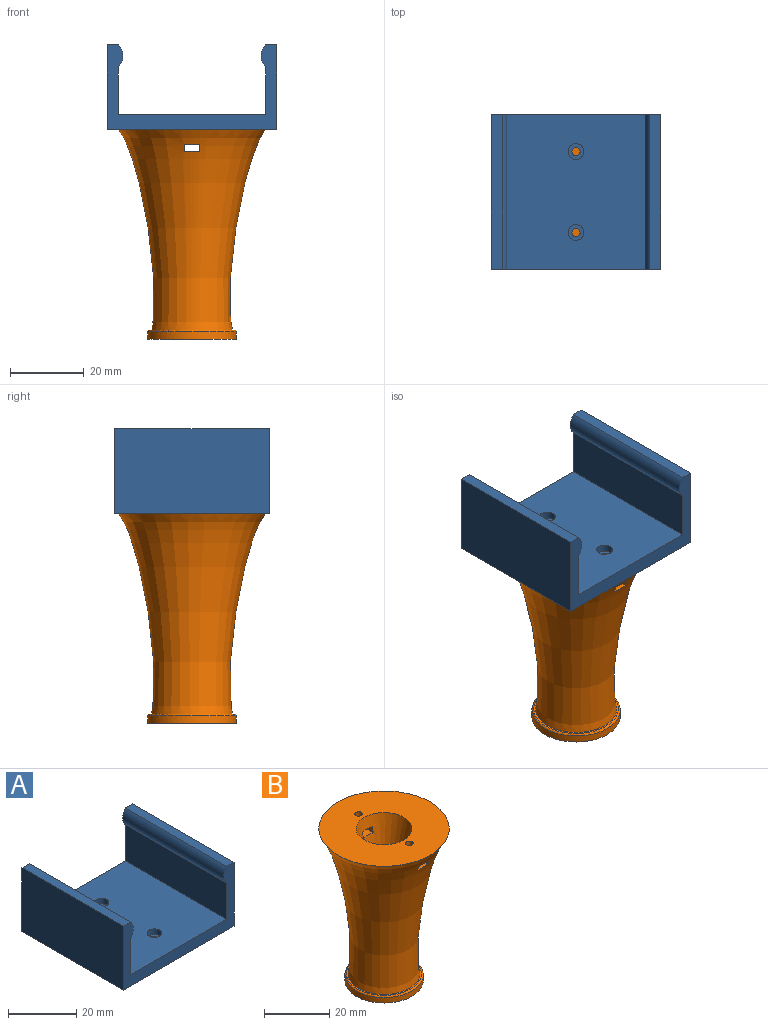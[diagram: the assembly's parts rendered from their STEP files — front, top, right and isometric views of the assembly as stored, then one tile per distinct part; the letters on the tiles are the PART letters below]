
ASSEMBLY  parts=2 mates=1
PART A: 18 faces, bbox 46x42x23 mm
  f0: cylinder r=1.1mm len=2.2mm, axis (0,0,1), area 13.8mm2, adj f2,f17
  f1: cylinder r=1.1mm len=2.2mm, axis (0,0,1), area 13.8mm2, adj f2,f15
  f2: plane 46x42mm, normal (0,0,-1), area 1924.4mm2, adj f0,f1,f3,f11,f12,f13
  f3: plane 42x23mm, normal (1,0,0), area 966mm2, adj f2,f4,f12,f13
  f4: plane 42x3mm, normal (0,0,1), area 126mm2, adj f3,f5,f12,f13
  f5: cylinder r=4.24mm len=42mm, axis (0,1,0), area 279.9mm2, adj f4,f6,f12,f13
  f6: plane 42x13mm, normal (-1,0,0), area 546mm2, adj f5,f7,f12,f13
  f7: plane 42x40mm, normal (0,0,1), area 1651mm2, adj f6,f8,f12,f13,f14,f16
  f8: plane 42x13mm, normal (1,0,0), area 546mm2, adj f7,f9,f12,f13
  f9: cylinder r=4.24mm len=42mm, axis (0,1,0), area 279.9mm2, adj f8,f10,f12,f13
  f10: plane 42x3mm, normal (0,0,1), area 126mm2, adj f9,f11,f12,f13
  f11: plane 42x23mm, normal (-1,0,0), area 966mm2, adj f2,f10,f12,f13
  f12: plane 46x23mm, normal (0,-1,0), area 308.3mm2, adj f2,f3,f4,f5,f6,f7,f8,f9
  f13: plane 46x23mm, normal (0,1,0), area 308.3mm2, adj f2,f3,f4,f5,f6,f7,f8,f9
  f14: cylinder r=2.15mm len=4.3mm, axis (0,0,1), area 27mm2, adj f7,f15
  f15: plane 4.3x4.3mm, normal (0,0,1), area 10.7mm2, adj f1,f14
  f16: cylinder r=2.15mm len=4.3mm, axis (0,0,1), area 27mm2, adj f7,f17
  f17: plane 4.3x4.3mm, normal (0,0,1), area 10.7mm2, adj f0,f16
PART B: 24 faces, bbox 40.1x40.1x57.1 mm
  f0: revolved ~54.5x40mm, area 4538.5mm2, adj f2,f3,f9,f10,f11,f12,f13,f14
  f1: cone r=8.53mm half-angle=13.6deg, axis (0,0,1), area 785.6mm2, adj f2,f6,f9,f10,f11,f12,f13,f14
  f2: plane 40x40mm, normal (0,0,1), area 1020mm2, adj f0,f1,f19,f20
  f3: plane 23x23mm, normal (0,0,1), area 34.8mm2, adj f0,f23
  f4: cylinder r=12mm len=24mm, axis (0,0,1), area 150.8mm2, adj f5,f23
  f5: plane 24x24mm, normal (0,0,-1), area 321.5mm2, adj f4,f8
  f6: cone r=3.56mm half-angle=9.2deg, axis (0,0,1), area 207.1mm2, adj f1,f7
  f7: cone r=1.46mm half-angle=4.7deg, axis (0,0,-1), area 111.7mm2, adj f6,f8
  f8: cone r=2.24mm half-angle=16.9deg, axis (0,0,-1), area 396mm2, adj f5,f7
  f9: plane 10.22x4.3mm, normal (0,0,1), area 38.6mm2, adj f0,f1,f10,f12,f21
  f10: plane 10.99x2.1mm, normal (1,0,0), area 20.4mm2, adj f0,f1,f9,f11
  f11: plane 10.51x4.3mm, normal (0,0,-1), area 40mm2, adj f0,f1,f10,f12,f20
  f12: plane 10.99x2.1mm, normal (-1,0,0), area 20.4mm2, adj f0,f1,f9,f11
  f13: plane 10.99x2.1mm, normal (-1,0,0), area 20.4mm2, adj f0,f1,f14,f16
  f14: plane 10.51x4.3mm, normal (0,0,-1), area 40mm2, adj f0,f1,f13,f15,f19
  f15: plane 10.99x2.1mm, normal (1,0,0), area 20.4mm2, adj f0,f1,f14,f16
  f16: plane 10.22x4.3mm, normal (0,0,1), area 38.6mm2, adj f0,f1,f13,f15,f18
  f17: plane 2.3x2.3mm, normal (0,0,1), area 4.2mm2, adj f18
  f18: cylinder r=1.15mm len=4mm, axis (0,0,1), area 28.9mm2, adj f16,f17
  f19: cylinder r=1.15mm len=4mm, axis (0,0,1), area 28.9mm2, adj f2,f14
  f20: cylinder r=1.15mm len=4mm, axis (0,0,1), area 28.9mm2, adj f2,f11
  f21: cylinder r=1.15mm len=4mm, axis (0,0,1), area 28.9mm2, adj f9,f22
  f22: plane 2.3x2.3mm, normal (0,0,1), area 4.2mm2, adj f21
  f23: torus R=11.5mm, axis (0,0,-1), area 58.3mm2, adj f3,f4
PLACE A t=(-27.6,3.1,25.55)mm
PLACE B t=(-27.6,-17.9,-31.45)mm
MATE fastened A.f0 <-> B.f18  axis (0,0,-1) through (-27.6,-28.9,25.55)mm
